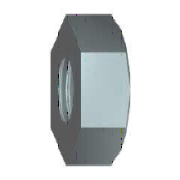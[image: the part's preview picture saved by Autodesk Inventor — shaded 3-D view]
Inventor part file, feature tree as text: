
AUTODESK INVENTOR PART (.ipt)
format: ipt  version: 2024.2 (Build 282272000, 272)  size: 196,608 bytes
history: native  units: mm (DEFAULTED — no unit token found)
features: plane x2, fillet x2, hole x1, chamfer x1, other x1, mirror x1, extrude x1, sketch x1
ambient origin geometry x7: Origin, YZ Plane, XZ Plane, X Axis, Y Axis, Z Axis, Center Point
bodies: Solid1 (feature_tree), Body (feature_tree)
feature tree (10):
  hole  "Thread"  [1 undecoded]
  chamfer  "Chamfer3"  Distance=5.5mm
  other  "Work Axis1"
  plane  "Work Plane1"
  plane  "Work Plane2"
  mirror  "Mirror1"
  extrude  "Extrusion2"  TaperAngle=30.0deg  [1 undecoded]
  fillet  "Fillet1"  [1 undecoded]
  fillet  "Fillet2"  Radius=0.270633mm
  sketch  "Sketch6"  dims[d0=6.350853mm d1=3.0mm d2=0.0mm d3=5.5mm d4=30.0deg d5=90.0deg d6=2.459mm d7=12.7mm d8=9.525mm d9=6.35mm d10=14.3117mm d11=19.05mm d12=20.594885mm d13=0.270633mm d14=30.0deg d20=0.0mm d21=0.270633mm d24=0.0mm d25=0.0mm d26=5.0mm d27=1.0mm d28=0.0mm d29=0.5mm d30=0.1mm]
note: 3 required parameter values undecoded (feature->parameter linkage not recoverable at this tier; creation-order binding heuristic only, values carry confidence <= 0.55)
